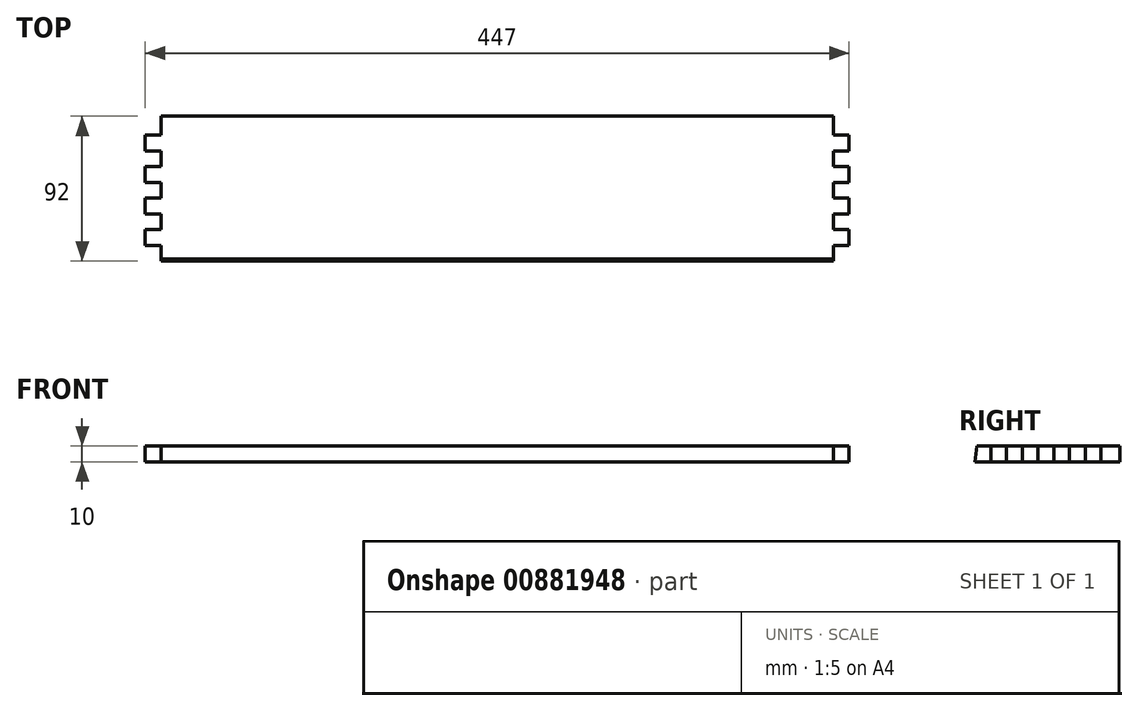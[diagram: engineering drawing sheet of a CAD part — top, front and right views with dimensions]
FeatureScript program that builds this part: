
annotation { "Feature Type Name" : "Feature", "Feature Type Description" : "" }
export const myFeature = defineFeature(function(context is Context, id is Id, definition is map)
    precondition{}
    {
        {
            var Q0;
            Q0=qCreatedBy(makeId("Top.planeOp"),FACE);
            var sketch = newSketch(context, id + "F0", { "sketchPlane" : qUnion([Q0])});
            skLineSegment(sketch, "E0.bottom", {"start": v(-145.63, 56.94) * mm, "end": v(301.37, 56.94) * mm});
            skLineSegment(sketch, "E0.top", {"start": v(-145.63, -33.06) * mm, "end": v(301.37, -33.06) * mm});
            skLineSegment(sketch, "E0.left", {"start": v(-145.63, 56.94) * mm, "end": v(-145.63, -33.06) * mm});
            skLineSegment(sketch, "E0.right", {"start": v(301.37, 56.94) * mm, "end": v(301.37, -33.06) * mm});
            skLineSegment(sketch, "E1.bottom", {"start": v(-145.63, 56.94) * mm, "end": v(-135.63, 56.94) * mm});
            skLineSegment(sketch, "E1.top", {"start": v(-145.63, -33.06) * mm, "end": v(-135.63, -33.06) * mm});
            skLineSegment(sketch, "E1.right", {"start": v(-135.63, 56.94) * mm, "end": v(-135.63, -33.06) * mm});
            skLineSegment(sketch, "E2.bottom", {"start": v(301.37, 56.94) * mm, "end": v(291.37, 56.94) * mm});
            skLineSegment(sketch, "E2.top", {"start": v(301.37, -33.06) * mm, "end": v(291.37, -33.06) * mm});
            skLineSegment(sketch, "E2.right", {"start": v(291.37, 56.94) * mm, "end": v(291.37, -33.06) * mm});
            skLineSegment(sketch, "E3.left", {"start": v(-145.63, 56.94) * mm, "end": v(-145.63, 46.94) * mm});
            skLineSegment(sketch, "E4.bottom", {"start": v(291.37, 56.94) * mm, "end": v(301.37, 56.94) * mm});
            skLineSegment(sketch, "E4.top", {"start": v(291.37, 46.94) * mm, "end": v(301.37, 46.94) * mm});
            skLineSegment(sketch, "E4.left", {"start": v(291.37, 56.94) * mm, "end": v(291.37, 46.94) * mm});
            skLineSegment(sketch, "E4.right", {"start": v(301.37, 56.94) * mm, "end": v(301.37, 46.94) * mm});
            skLineSegment(sketch, "E5.MirrorCS", {"start": v(301.37, 36.94) * mm, "end": v(291.37, 36.94) * mm});
            skLineSegment(sketch, "E6.MirrorCS", {"start": v(291.37, 26.94) * mm, "end": v(301.37, 26.94) * mm});
            skLineSegment(sketch, "E7.MirrorCS", {"start": v(301.37, 16.94) * mm, "end": v(291.37, 16.94) * mm});
            skLineSegment(sketch, "E8.MirrorCS", {"start": v(291.37, 6.94) * mm, "end": v(301.37, 6.94) * mm});
            skLineSegment(sketch, "E9.MirrorCS", {"start": v(301.37, -3.06) * mm, "end": v(291.37, -3.06) * mm});
            skLineSegment(sketch, "E10.MirrorCS", {"start": v(291.37, -13.06) * mm, "end": v(301.37, -13.06) * mm});
            skLineSegment(sketch, "E11.top", {"start": v(-145.63, 46.94) * mm, "end": v(-135.63, 46.94) * mm});
            skLineSegment(sketch, "E11.right", {"start": v(-135.63, 56.94) * mm, "end": v(-135.63, 46.94) * mm});
            skLineSegment(sketch, "E12.MirrorCS", {"start": v(-145.63, 36.94) * mm, "end": v(-135.63, 36.94) * mm});
            skLineSegment(sketch, "E13.MirrorCS", {"start": v(-145.63, 26.94) * mm, "end": v(-135.63, 26.94) * mm});
            skLineSegment(sketch, "E14.MirrorCS", {"start": v(-145.63, 16.94) * mm, "end": v(-135.63, 16.94) * mm});
            skLineSegment(sketch, "E15.MirrorCS", {"start": v(-145.63, 6.94) * mm, "end": v(-135.63, 6.94) * mm});
            skLineSegment(sketch, "E16.MirrorCS", {"start": v(-145.63, -3.06) * mm, "end": v(-135.63, -3.06) * mm});
            skLineSegment(sketch, "E17.MirrorCS", {"start": v(-145.63, -13.06) * mm, "end": v(-135.63, -13.06) * mm});
            skLineSegment(sketch, "E18.MirrorCS", {"start": v(-145.63, -23.06) * mm, "end": v(-135.63, -23.06) * mm});
            skLineSegment(sketch, "E19.MirrorCS", {"start": v(301.37, -23.06) * mm, "end": v(291.37, -23.06) * mm});
            skLineSegment(sketch, "E20.bottom", {"start": v(-135.63, 56.94) * mm, "end": v(291.37, 56.94) * mm});
            skLineSegment(sketch, "E20.top", {"start": v(-135.63, 58.94) * mm, "end": v(291.37, 58.94) * mm});
            skLineSegment(sketch, "E20.left", {"start": v(-135.63, 56.94) * mm, "end": v(-135.63, 58.94) * mm});
            skLineSegment(sketch, "E20.right", {"start": v(291.37, 56.94) * mm, "end": v(291.37, 58.94) * mm});
            skSolve(sketch);
        }
        {
            var Q0;
            {var subQ0=sQuery(id+"F0.wireOp",EDGE,"E1.right");var subQ1=sQuery(id+"F0.wireOp",EDGE,"E0.bottom");var subQ2=makeQuery(id+"F0.imprint","INTERSECT",VERTEX,{"derivedFrom":[subQ1,subQ0]});Q0=makeQuery(id+"F0.imprint","IMPRINT",FACE,{"disambiguationData":[TD([[makeQuery(id+"F0.imprint","IMPRINT",EDGE,{"disambiguationData":[TD([[subQ2,-1.0]])],"derivedFrom":subQ1}),-1.0]])]});}
            var Q1;
            {var subQ0=sQuery(id+"F0.wireOp",EDGE,"E11.top");Q1=makeQuery(id+"F0.imprint","IMPRINT",FACE,{"disambiguationData":[TD([[makeQuery(id+"F0.imprint","IMPRINT",EDGE,{"derivedFrom":subQ0}),-1.0]])]});}
            var Q2;
            {var subQ0=sQuery(id+"F0.wireOp",EDGE,"E13.MirrorCS");Q2=makeQuery(id+"F0.imprint","IMPRINT",FACE,{"disambiguationData":[TD([[makeQuery(id+"F0.imprint","IMPRINT",EDGE,{"derivedFrom":subQ0}),-1.0]])]});}
            var Q3;
            {var subQ0=sQuery(id+"F0.wireOp",EDGE,"E15.MirrorCS");Q3=makeQuery(id+"F0.imprint","IMPRINT",FACE,{"disambiguationData":[TD([[makeQuery(id+"F0.imprint","IMPRINT",EDGE,{"derivedFrom":subQ0}),-1.0]])]});}
            var Q4;
            {var subQ0=sQuery(id+"F0.wireOp",EDGE,"E17.MirrorCS");Q4=makeQuery(id+"F0.imprint","IMPRINT",FACE,{"disambiguationData":[TD([[makeQuery(id+"F0.imprint","IMPRINT",EDGE,{"derivedFrom":subQ0}),-1.0]])]});}
            var Q5;
            {var subQ0=sQuery(id+"F0.wireOp",EDGE,"E4.top");Q5=makeQuery(id+"F0.imprint","IMPRINT",FACE,{"disambiguationData":[TD([[makeQuery(id+"F0.imprint","IMPRINT",EDGE,{"derivedFrom":subQ0}),-1.0]])]});}
            var Q6;
            {var subQ0=sQuery(id+"F0.wireOp",EDGE,"E6.MirrorCS");Q6=makeQuery(id+"F0.imprint","IMPRINT",FACE,{"disambiguationData":[TD([[makeQuery(id+"F0.imprint","IMPRINT",EDGE,{"derivedFrom":subQ0}),-1.0]])]});}
            var Q7;
            {var subQ0=sQuery(id+"F0.wireOp",EDGE,"E8.MirrorCS");Q7=makeQuery(id+"F0.imprint","IMPRINT",FACE,{"disambiguationData":[TD([[makeQuery(id+"F0.imprint","IMPRINT",EDGE,{"derivedFrom":subQ0}),-1.0]])]});}
            var Q8;
            {var subQ0=sQuery(id+"F0.wireOp",EDGE,"E10.MirrorCS");Q8=makeQuery(id+"F0.imprint","IMPRINT",FACE,{"disambiguationData":[TD([[makeQuery(id+"F0.imprint","IMPRINT",EDGE,{"derivedFrom":subQ0}),-1.0]])]});}
            var Q9;
            Q9=makeQuery(id+"F0.imprint","IMPRINT",FACE,{"disambiguationData":[TD([[makeQuery(id+"F0.imprint","IMPRINT",EDGE,{"derivedFrom":sQuery(id+"F0.wireOp",EDGE,"E20.top")}),-1.0]])]});
            extrude(context, id + "F1", {"entities" : qUnion([Q0, Q1, Q2, Q3, Q4, Q5, Q6, Q7, Q8, Q9]), "depth" : 10 * mm, "offsetDistance" : 25 * mm});
        }
        {
            var Q0;
            {var subQ0=sQuery(id+"F0.wireOp",EDGE,"E2.right");Q0=makeQuery(id+"F1.opExtrude","SWEPT_FACE",FACE,{"disambiguationData":[OSD([subQ0]),TDD([makeQuery(id+"F0.imprint","IMPRINT",EDGE,{"disambiguationData":[TD([[makeQuery(id+"F0.imprint","INTERSECT",VERTEX,{"derivedFrom":[sQuery(id+"F0.wireOp",EDGE,"E0.top"),subQ0]}),1.0]])],"derivedFrom":subQ0})])]});}
            var sketch = newSketch(context, id + "F2", { "sketchPlane" : qUnion([Q0])});
            skLineSegment(sketch, "E21", {"start": v(-33.06, 0) * mm, "end": v(-31.75, 10) * mm});
            skLineSegment(sketch, "E22", {"start": v(-31.75, 10) * mm, "end": v(-33.06, 10) * mm});
            skLineSegment(sketch, "E23", {"start": v(-33.06, 10) * mm, "end": v(-33.06, 0) * mm});
            skLineSegment(sketch, "E24", {"start": v(-31.75, 10) * mm, "end": v(-31.75, 19.56) * mm});
            skLineSegment(sketch, "E25", {"start": v(-31.75, 19.56) * mm, "end": v(58.94, 10) * mm});
            skLineSegment(sketch, "E26", {"start": v(58.94, 10) * mm, "end": v(-31.75, 10) * mm});
            skSolve(sketch);
        }
        {
            var Q0;
            Q0 = qSketchRegion(id + "F2", true);
            extrude(context, id + "F3", {"entities" : qUnion([Q0]), "operationType" : NewBodyOperationType.REMOVE, "oppositeDirection" : true, "depth" : 427 * mm, "offsetDistance" : 25 * mm});
        }
    });
